# Revit family: PRD_AR_ShwrFttngsPckg_F5EElectronicThermostaticMixer_F5ET2031_F5ET2040
name_source: partatom
category: Plumbing Fixtures
units: mm (PartAtom-declared; Revit-internal decimal feet)

## family parameters
Cut with Voids When Loaded = No
Enable Cutting in Views = No
Host = Face
Maintain Annotation Orientation = No
OmniClass Number = 23.45.05.14.99
OmniClass Title = Other Sanitary Washing Plumbing Fixtures
Part Type = Normal
Room Calculation Point = No
Round Connector Dimension = Use Diameter
Shared = No

## types (2) — shared parameters
AccentColour = chrome-look (glossy)
AdditionalConnections = No
AdjustableFlowTime = Yes
AssetType = Fixed
BasicColour = stainless steel-look
BodyMaterial = PRD_AR_StainlessSteel_SatinFinished
BuiltInFittingModel = Finishing section
CalculationFlowRateColdWater = 0.15 l/s
CalculationFlowRateHotWater = 0.15 l/s
Category = Pr_40_20_87_75, Shower fittings package
Circulation = No
Color = stainless steel-look
CompatibleA3000Open = Yes
CoverPlateHeight = 245 mm
CoverPlateWidth = 190 mm
DN = 15  [stored 0.0492126 ft]
Default Elevation = 1200 mm
DefaultAutomaticHygieneFlush = 24h after the last activity
DefaultFlowTime = 30 Seconds
DiameterNominal = DN 15
DrainSize = 15 mm  [stored 0.0492126 ft]
Export Type to IFC As = IfcSanitaryTerminalType
Finish = Satin finished
FlowColdWater = 0.2 L/s
FlowHotWater = 0.2 L/s
ForHandShower = No
FunctionalPrinciple = electronic self-closing
HasTray = No
HygieneFlushing = Yes
IfcExportAs = IfcSanitaryTerminalType
IfcExportType = SHOWER
InletSize = G 3/4 B
LockingMechanism = Top section, non-ceramic
Manufacturer = KWC Group Management AG
ManufacturerName = KWC Group Management AG
ManufacturerURL = www.kwc-professional.com
Material = stainless steel
MaterialCasing = stainless steel
MaterialFitting = brass-look
MaximumFlowTime = 255 Seconds
MinimumFlowPressure = 1 bar
MinimumFlowTime = 1 Seconds
NBSDescription = Shower fittings package
NBSReference = 45-35-70/330
NominalHeight = 245 mm  [stored 0.803806 ft]
NominalLength = 245 mm  [stored 0.803806 ft]
NominalWidth = 190 mm  [stored 0.62336 ft]
PositionOfPowerConnection = from top
PositionOfWaterConnection = from side
ProductInformation = http://pim.kwc.com
ProtectiveShutdown = Yes
ProtectiveSystemIP = IP59K
ShowerPipeDraining = No
ShowerType = Individual
Size = 15
SoundInsulation = No
Status = NEW
SurfaceFinishCasing = satin finished
SurfaceFinishFitting = chromed
SurfaceTreatmentFitting = Polished
TemperatureLimit = Yes
Type IFC Predefined Type = SHOWER
TypeOfMixing = with thermostat
TypeOfMounting = in-wall installation with box
TypeOfOperation = sensor operation
TypeOfPowerSupply = Transformer
TypeOfSensor = opto-electronic sensor
TypeOfShower = in-wall fitting
URL = www.kwc-professional.com
Uniclass2015Code = Pr_40_20_87_75
Uniclass2015Title = Shower fittings package
Uniclass2015Version = Products v1.36
Version = 1
VolumeFlowRateAt3Bar = 0.23 l/s
VolumeFlowRateBypassPWH = 0.05 l/s
WaterConnection = threaded connection (external)
WithBackflowPreventer = Yes
WithFilter = Yes
WithRosettesCoverPlate = Yes
WithTransformerPowerSupply = No
zero-valued in all types: NominalDepth

## per-type parameters (varying)
| type | BIMObjectName | Battery | ConnectionWithPayWaterDispenser | Description | Features | ModelNumber | Name | Parameterization | PowerConsumption | PowerSupplyConnection | ThermalDisinfection |
| F5ET2031 | PRD_AR_ ShowerFittingsPackage_F5EElectronicThermostaticMixer_F5ET2031 | No | via electronic module | F5E-Therm thermostatic mixer DN 15 as finished installation kit for wall mounting in mounting material, for shower facilities. Electrically controlled, connects to hot water and cold water. Function block with integrated solenoid valve cartridge, thermostat and mechanism for two optional bypass solenoid valve cartridges for separate rinsing of the cold-water line and implementation of program-controlled thermal disinfection as well as for separate sampling of cold or hot water. Thermostat with metal handle with adjustable and turn-proof temperature stop and option for manual thermal disinfection. All-metal construction, visible parts high-polished, chrome-plated. With holding frame and profile seal, stainless-steel cover plate 190x 245 mm with covered screw fixing including sensor with control electronics, rosette, backflow preventers and strainers. Depth adjustability 25 mm. Activated hygiene flushing 24 hours after last activation and storage of statistical data. With option for parameterization and communication via optional, bidirectional remote control. Optionally for battery operation with 6 V lithium battery (CR-P2) per fitting or separate power supply via power supply unit 6.75 V/12 V DC or AQUA 3000 open system accessories. Battery compartment including battery or power supply unit with extension cable must be ordered separately. | Electrically controlled, connects to hot water and cold water. All-metal construction, visible parts high-polished, chrome-plated. Depth adjustability 25 mm. Battery compartment including battery or power supply unit with extension cable must be ordered separately. | 2030067151 | F5E Electronic thermostatic mixer F5ET2031 | remote control | 1.5 Voltampere | 6,75 / 12 V DC / A3000 open | Yes |
| F5ET2040 | PRD_AR_ ShowerFittingsPackage_F5EElectronicThermostaticMixer_F5ET2040 | Yes | single / multiple pay water dispenser | F5E-Therm - A3000 open thermostatic mixer DN 15 as finished installation kit for in-wall installation in basic installation kit, for shower facilities. Electrically controlled, connects to hot water and cold water. Function block with integrated solenoid valve cartridge, thermostat and two bypass solenoid valve cartridges for separate rinsing of the cold-water line and implementation of program-controlled thermal disinfection as well as for separate sampling of cold or hot water. Thermostat with metal handle with adjustable and turn-proof temperature stop and option for manual thermal disinfection. All-metal construction, visible parts high-polished, chrome-plated. With holding frame with profile seal, 190 x 245 mm stainless steel cover plate with covered screw fixing including touch sensor with control electronics, start/stop function, rosette, water tight electronic module and electric T-junction for connection to system cables, backflow preventers and strainers. Depth adjustability 25 mm. Activated hygiene flushing 24 hours after the last activity. External control unit, like valve setting, cleaning deactivation, storage of statistical data and communication via ECC2 function controller, 24 V DC. | Electrically controlled, connects to hot water and cold water. All-metal construction, visible parts high-polished, chrome-plated. Depth adjustability 25 mm. | 2030071563 | F5E Electronic thermostatic mixer F5ET2040 | network |  | A3000 open 24 V DC | automatic thermal disinfection |

note: column(s) folded — value = type name in every type: Model, ModelReference

note: [stored X ft] marks values corroborated as IEEE doubles in the binary element streams (Revit-internal decimal feet)

## geometry (parser evidence)
native form markers: Sweep x5
no freeform markers — native parametric forms only
